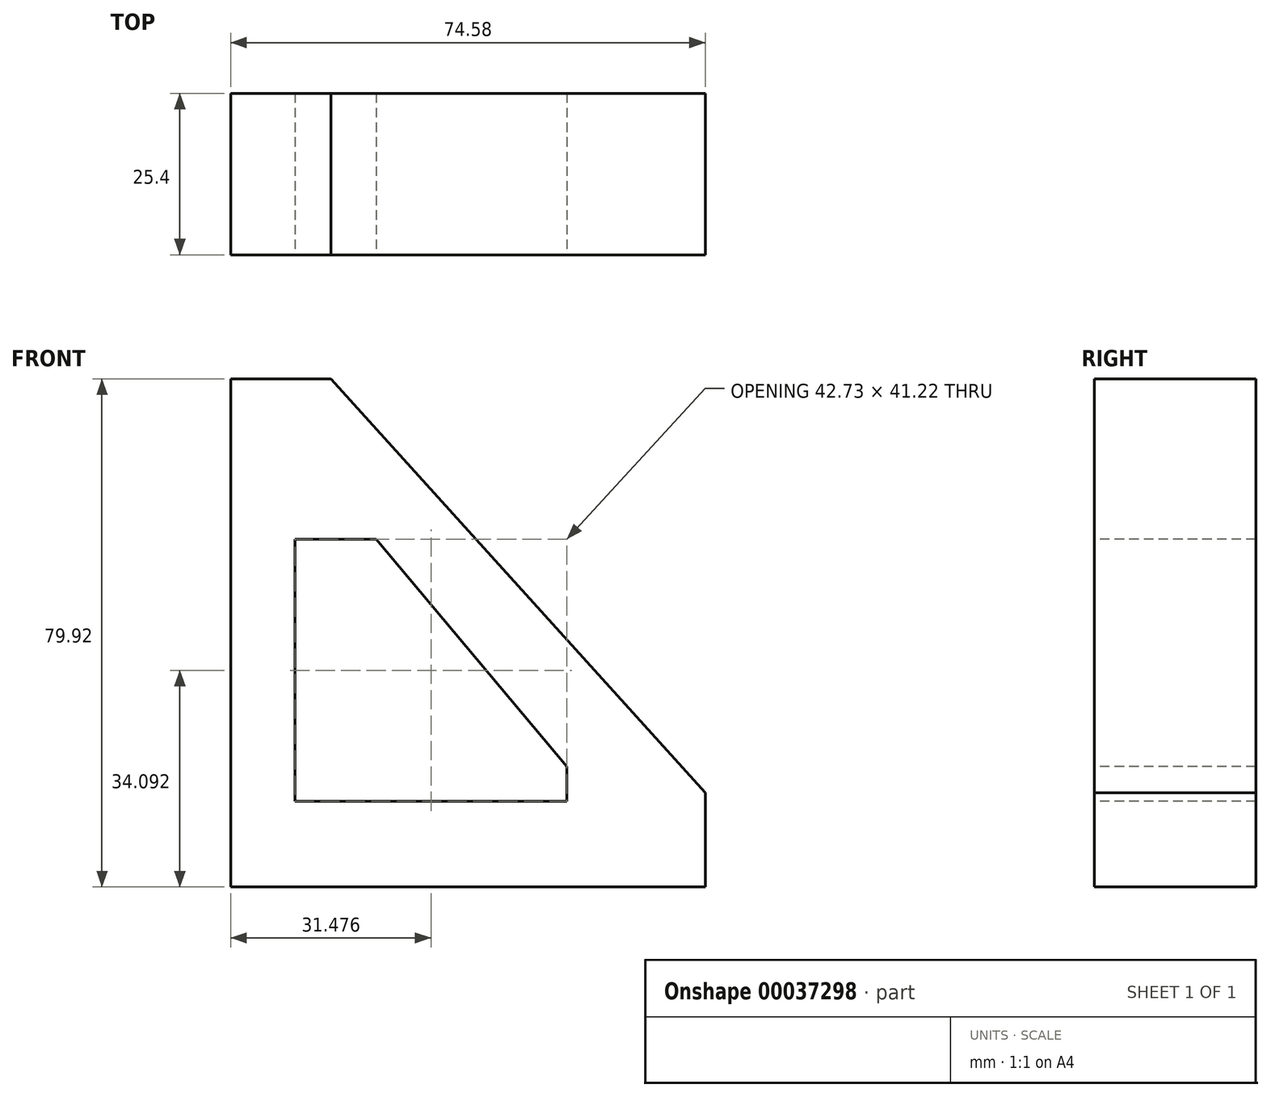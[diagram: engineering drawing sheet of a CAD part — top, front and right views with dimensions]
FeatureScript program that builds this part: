
annotation { "Feature Type Name" : "Feature", "Feature Type Description" : "" }
export const myFeature = defineFeature(function(context is Context, id is Id, definition is map)
    precondition{}
    {
        {
            var Q0;
            Q0=qCreatedBy(makeId("Front.planeOp"),FACE);
            var sketch = newSketch(context, id + "F0", { "sketchPlane" : qUnion([Q0])});
            skLineSegment(sketch, "E0", {"start": v(-44.66, 44) * mm, "end": v(-44.66, -35.91) * mm});
            skLineSegment(sketch, "E1", {"start": v(-44.66, -35.91) * mm, "end": v(29.92, -35.91) * mm});
            skLineSegment(sketch, "E2", {"start": v(29.92, -35.91) * mm, "end": v(29.92, -21.11) * mm});
            skLineSegment(sketch, "E3", {"start": v(-44.66, 44) * mm, "end": v(-28.9, 44) * mm});
            skLineSegment(sketch, "E4", {"start": v(-28.9, 44) * mm, "end": v(29.92, -21.11) * mm});
            skSolve(sketch);
        }
        {
            var Q0;
            Q0=makeQuery(id+"F0.imprint","IMPRINT",FACE,{"disambiguationData":[TD([[makeQuery(id+"F0.imprint","IMPRINT",EDGE,{"derivedFrom":sQuery(id+"F0.wireOp",EDGE,"E0")}),1.0]])]});
            extrude(context, id + "F1", {"entities" : qUnion([Q0]), "depth" : 25.4 * mm});
        }
        {
            var Q0;
            Q0=makeQuery(id+"F1.opExtrude","CAP_FACE",FACE,{"disambiguationData":[OSD([sQuery(id+"F0.wireOp",EDGE,"E0"),sQuery(id+"F0.wireOp",EDGE,"E1"),sQuery(id+"F0.wireOp",EDGE,"E2"),sQuery(id+"F0.wireOp",EDGE,"E3"),sQuery(id+"F0.wireOp",EDGE,"E4")])],"isStart":false});
            var sketch = newSketch(context, id + "F2", { "sketchPlane" : qUnion([Q0])});
            skLineSegment(sketch, "E5", {"start": v(-34.55, 18.8) * mm, "end": v(-34.55, -22.43) * mm});
            skLineSegment(sketch, "E6", {"start": v(-34.55, -22.43) * mm, "end": v(8.18, -22.43) * mm});
            skLineSegment(sketch, "E7", {"start": v(8.18, -22.43) * mm, "end": v(8.18, -16.97) * mm});
            skLineSegment(sketch, "E8", {"start": v(8.18, -16.97) * mm, "end": v(-21.82, 18.8) * mm});
            skLineSegment(sketch, "E9", {"start": v(-21.82, 18.8) * mm, "end": v(-34.55, 18.8) * mm});
            skSolve(sketch);
        }
        {
            var Q0;
            Q0 = qSketchRegion(id + "F2", true);
            extrude(context, id + "F3", {"entities" : qUnion([Q0]), "operationType" : NewBodyOperationType.REMOVE, "endBound" : BoundingType.THROUGH_ALL, "oppositeDirection" : true, "depth" : 25.4 * mm});
        }
    });
